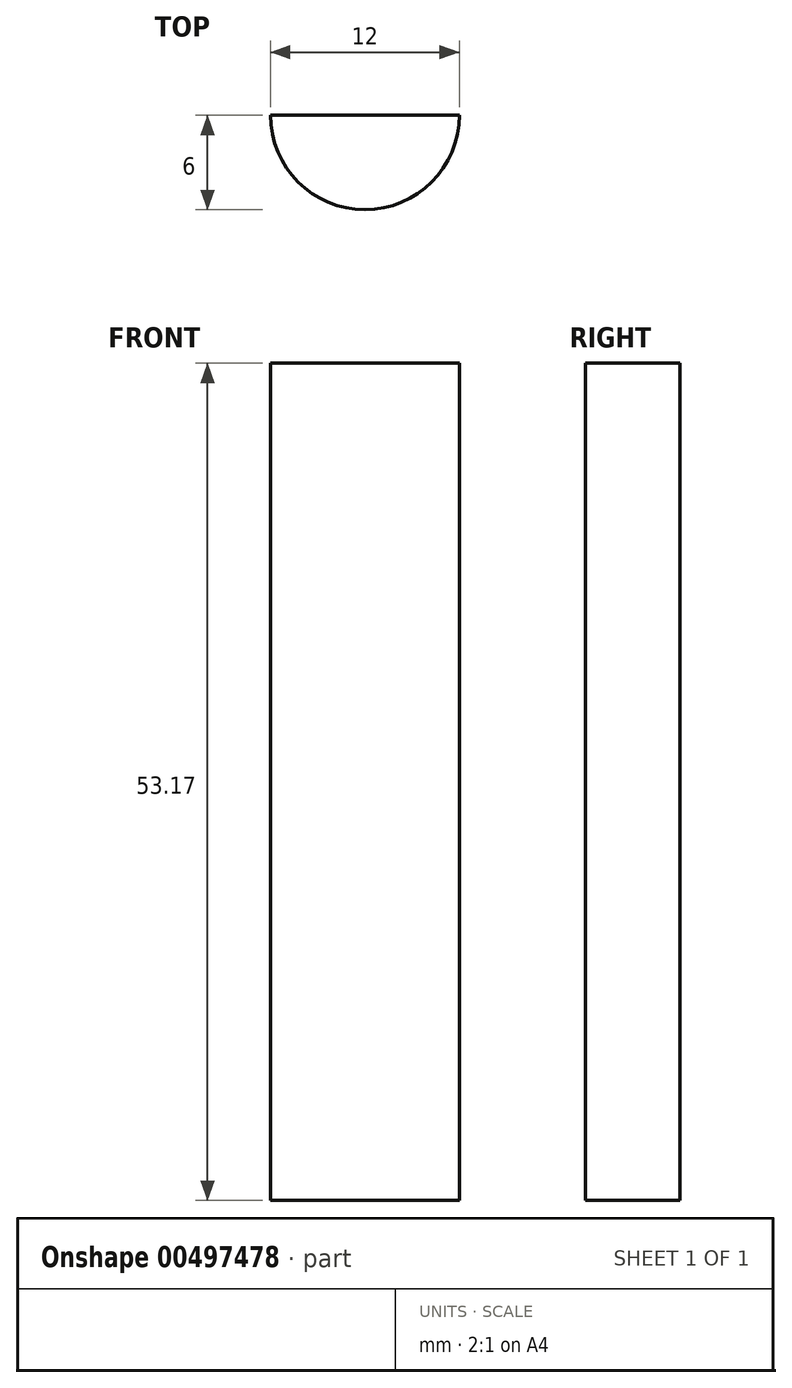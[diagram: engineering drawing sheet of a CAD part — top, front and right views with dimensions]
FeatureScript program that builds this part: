
annotation { "Feature Type Name" : "Feature", "Feature Type Description" : "" }
export const myFeature = defineFeature(function(context is Context, id is Id, definition is map)
    precondition{}
    {
        {
            var Q0;
            Q0=qCreatedBy(makeId("Top.planeOp"),FACE);
            var sketch = newSketch(context, id + "F0", { "sketchPlane" : qUnion([Q0])});
            skLineSegment(sketch, "E0", {"start": v(0, 60) * mm, "end": v(0, -60) * mm});
            skLineSegment(sketch, "E1", {"start": v(-70, 0) * mm, "end": v(70, 0) * mm});
            skCircle(sketch, "E2", {"center": v(0, 0) * mm, "radius": 3.37 * mm});
            skCircle(sketch, "E3", {"center": v(0, 0) * mm, "radius": 6 * mm});
            skSolve(sketch);
        }
        {
            var Q0;
            {var subQ0=sQuery(id+"F0.wireOp",EDGE,"E3");var subQ1=sQuery(id+"F0.wireOp",EDGE,"E0");var subQ2=makeQuery(id+"F0.imprint","INTERSECT",VERTEX,{"disambiguationData":[OD(0.0)],"derivedFrom":[subQ1,subQ0]});Q0=makeQuery(id+"F0.imprint","IMPRINT",FACE,{"disambiguationData":[TD([[makeQuery(id+"F0.imprint","IMPRINT",EDGE,{"disambiguationData":[TD([[subQ2,-1.0]])],"derivedFrom":subQ1}),-1.0]])]});}
            var Q1;
            {var subQ0=sQuery(id+"F0.wireOp",EDGE,"E2");var subQ1=sQuery(id+"F0.wireOp",EDGE,"E0");var subQ2=makeQuery(id+"F0.imprint","INTERSECT",VERTEX,{"disambiguationData":[OD(0.0)],"derivedFrom":[subQ1,subQ0]});Q1=makeQuery(id+"F0.imprint","IMPRINT",FACE,{"disambiguationData":[TD([[makeQuery(id+"F0.imprint","IMPRINT",EDGE,{"disambiguationData":[TD([[subQ2,-1.0]])],"derivedFrom":subQ1}),-1.0]])]});}
            var Q2;
            {var subQ0=sQuery(id+"F0.wireOp",EDGE,"E2");var subQ1=sQuery(id+"F0.wireOp",EDGE,"E0");var subQ2=makeQuery(id+"F0.imprint","INTERSECT",VERTEX,{"disambiguationData":[OD(0.0)],"derivedFrom":[subQ1,subQ0]});Q2=makeQuery(id+"F0.imprint","IMPRINT",FACE,{"disambiguationData":[TD([[makeQuery(id+"F0.imprint","IMPRINT",EDGE,{"disambiguationData":[TD([[subQ2,-1.0]])],"derivedFrom":subQ1}),1.0]])]});}
            var Q3;
            {var subQ0=sQuery(id+"F0.wireOp",EDGE,"E3");var subQ1=sQuery(id+"F0.wireOp",EDGE,"E0");var subQ2=makeQuery(id+"F0.imprint","INTERSECT",VERTEX,{"disambiguationData":[OD(0.0)],"derivedFrom":[subQ1,subQ0]});Q3=makeQuery(id+"F0.imprint","IMPRINT",FACE,{"disambiguationData":[TD([[makeQuery(id+"F0.imprint","IMPRINT",EDGE,{"disambiguationData":[TD([[subQ2,-1.0]])],"derivedFrom":subQ1}),1.0]])]});}
            var Q4;
            {var subQ0=sQuery(id+"F0.wireOp",EDGE,"E3");var subQ1=sQuery(id+"F0.wireOp",EDGE,"E0");var subQ2=makeQuery(id+"F0.imprint","INTERSECT",VERTEX,{"disambiguationData":[OD(1.0)],"derivedFrom":[subQ1,subQ0]});Q4=makeQuery(id+"F0.imprint","IMPRINT",FACE,{"disambiguationData":[TD([[makeQuery(id+"F0.imprint","IMPRINT",EDGE,{"disambiguationData":[TD([[subQ2,1.0]])],"derivedFrom":subQ1}),1.0]])]});}
            var Q5;
            {var subQ0=sQuery(id+"F0.wireOp",EDGE,"E1");var subQ1=sQuery(id+"F0.wireOp",EDGE,"E0");var subQ2=makeQuery(id+"F0.imprint","INTERSECT",VERTEX,{"derivedFrom":[subQ1,subQ0]});Q5=makeQuery(id+"F0.imprint","IMPRINT",FACE,{"disambiguationData":[TD([[makeQuery(id+"F0.imprint","IMPRINT",EDGE,{"disambiguationData":[TD([[subQ2,-1.0]])],"derivedFrom":subQ1}),1.0]])]});}
            var Q6;
            {var subQ0=sQuery(id+"F0.wireOp",EDGE,"E1");var subQ1=sQuery(id+"F0.wireOp",EDGE,"E0");var subQ2=makeQuery(id+"F0.imprint","INTERSECT",VERTEX,{"derivedFrom":[subQ1,subQ0]});Q6=makeQuery(id+"F0.imprint","IMPRINT",FACE,{"disambiguationData":[TD([[makeQuery(id+"F0.imprint","IMPRINT",EDGE,{"disambiguationData":[TD([[subQ2,-1.0]])],"derivedFrom":subQ1}),-1.0]])]});}
            var Q7;
            {var subQ0=sQuery(id+"F0.wireOp",EDGE,"E3");var subQ1=sQuery(id+"F0.wireOp",EDGE,"E0");var subQ2=makeQuery(id+"F0.imprint","INTERSECT",VERTEX,{"disambiguationData":[OD(1.0)],"derivedFrom":[subQ1,subQ0]});Q7=makeQuery(id+"F0.imprint","IMPRINT",FACE,{"disambiguationData":[TD([[makeQuery(id+"F0.imprint","IMPRINT",EDGE,{"disambiguationData":[TD([[subQ2,1.0]])],"derivedFrom":subQ1}),-1.0]])]});}
            extrude(context, id + "F1", {"entities" : qUnion([Q0, Q1, Q2, Q3, Q4, Q5, Q6, Q7]), "oppositeDirection" : true, "depth" : (6.35 / 2) * mm});
        }
        {
            var Q0;
            Q0=qCreatedBy(makeId("Top.planeOp"),FACE);
            var sketch = newSketch(context, id + "F2", { "sketchPlane" : qUnion([Q0])});
            skLineSegment(sketch, "E4", {"start": v(0, 60) * mm, "end": v(0, -60) * mm});
            skLineSegment(sketch, "E5", {"start": v(-70, 0) * mm, "end": v(70, 0) * mm});
            skCircle(sketch, "E6", {"center": v(0, 0) * mm, "radius": 3.37 * mm});
            skCircle(sketch, "E7", {"center": v(0, 0) * mm, "radius": 6 * mm});
            skSolve(sketch);
        }
        {
            var Q0;
            {var subQ0=sQuery(id+"F2.wireOp",EDGE,"E6");var subQ1=sQuery(id+"F2.wireOp",EDGE,"E4");var subQ2=makeQuery(id+"F2.imprint","INTERSECT",VERTEX,{"disambiguationData":[OD(0.0)],"derivedFrom":[subQ1,subQ0]});Q0=makeQuery(id+"F2.imprint","IMPRINT",FACE,{"disambiguationData":[TD([[makeQuery(id+"F2.imprint","IMPRINT",EDGE,{"disambiguationData":[TD([[subQ2,-1.0]])],"derivedFrom":subQ1}),1.0]])]});}
            var Q1;
            {var subQ0=sQuery(id+"F2.wireOp",EDGE,"E5");var subQ1=sQuery(id+"F2.wireOp",EDGE,"E4");var subQ2=makeQuery(id+"F2.imprint","INTERSECT",VERTEX,{"derivedFrom":[subQ1,subQ0]});Q1=makeQuery(id+"F2.imprint","IMPRINT",FACE,{"disambiguationData":[TD([[makeQuery(id+"F2.imprint","IMPRINT",EDGE,{"disambiguationData":[TD([[subQ2,-1.0]])],"derivedFrom":subQ1}),1.0]])]});}
            var Q2;
            {var subQ0=sQuery(id+"F2.wireOp",EDGE,"E5");var subQ1=sQuery(id+"F2.wireOp",EDGE,"E4");var subQ2=makeQuery(id+"F2.imprint","INTERSECT",VERTEX,{"derivedFrom":[subQ1,subQ0]});Q2=makeQuery(id+"F2.imprint","IMPRINT",FACE,{"disambiguationData":[TD([[makeQuery(id+"F2.imprint","IMPRINT",EDGE,{"disambiguationData":[TD([[subQ2,-1.0]])],"derivedFrom":subQ1}),-1.0]])]});}
            var Q3;
            {var subQ0=sQuery(id+"F2.wireOp",EDGE,"E6");var subQ1=sQuery(id+"F2.wireOp",EDGE,"E4");var subQ2=makeQuery(id+"F2.imprint","INTERSECT",VERTEX,{"disambiguationData":[OD(0.0)],"derivedFrom":[subQ1,subQ0]});Q3=makeQuery(id+"F2.imprint","IMPRINT",FACE,{"disambiguationData":[TD([[makeQuery(id+"F2.imprint","IMPRINT",EDGE,{"disambiguationData":[TD([[subQ2,-1.0]])],"derivedFrom":subQ1}),-1.0]])]});}
            extrude(context, id + "F3", {"entities" : qUnion([Q0, Q1, Q2, Q3]), "operationType" : NewBodyOperationType.ADD, "depth" : 50 * mm});
        }
    });
